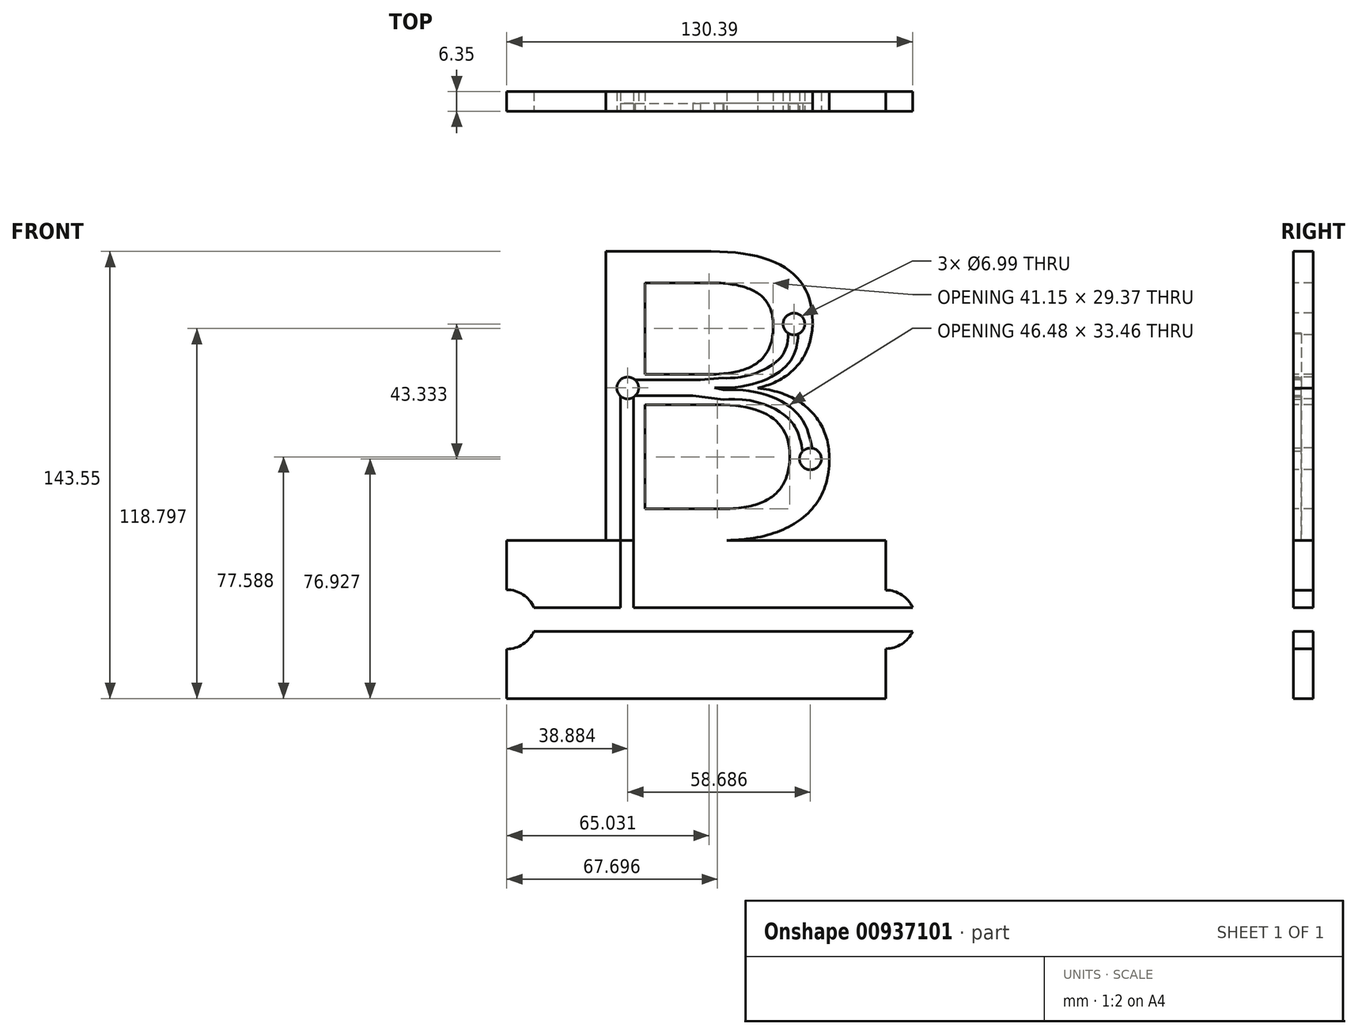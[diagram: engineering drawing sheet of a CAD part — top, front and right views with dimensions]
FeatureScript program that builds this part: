
annotation { "Feature Type Name" : "Feature", "Feature Type Description" : "" }
export const myFeature = defineFeature(function(context is Context, id is Id, definition is map)
    precondition{}
    {
        {
            var Q0;
            Q0=qCreatedBy(makeId("Front.planeOp"),FACE);
            var sketch = newSketch(context, id + "F0", { "sketchPlane" : qUnion([Q0])});
            skText(sketch, "E0", { "text": "B", "fontName": "Arimo-Regular.ttf"});
            skLineSegment(sketch, "E1", {"start": v(-24.82, -55) * mm, "end": v(-66.9, -55) * mm});
            skLineSegment(sketch, "E2", {"start": v(-66.9, -55) * mm, "end": v(-66.9, -70.87) * mm});
            skLineSegment(sketch, "E3", {"start": v(-66.9, -105.8) * mm, "end": v(54.89, -105.8) * mm});
            skLineSegment(sketch, "E4", {"start": v(54.89, -105.8) * mm, "end": v(54.89, -89.79) * mm});
            skLineSegment(sketch, "E5", {"start": v(54.89, -55) * mm, "end": v(0, -55) * mm});
            skArc(sketch, "E6", {"start": v(-66.9, -89.92) * mm, "mid": v(-57.38, -80.4) * mm, "end": v(-66.9, -70.87) * mm});
            skLineSegment(sketch, "E7.trimOffspring", {"start": v(-66.9, -89.92) * mm, "end": v(-66.9, -105.8) * mm});
            skArc(sketch, "E8", {"start": v(54.89, -89.79) * mm, "mid": v(64.29, -80.4) * mm, "end": v(54.89, -71) * mm});
            skLineSegment(sketch, "E9.trimOffspring", {"start": v(54.89, -71) * mm, "end": v(54.89, -55) * mm});
            skCircle(sketch, "E10", {"center": v(-28.03, -6.07) * mm, "radius": 3.5 * mm});
            skCircle(sketch, "E11", {"center": v(30.66, -28.86) * mm, "radius": 3.5 * mm});
            skCircle(sketch, "E12", {"center": v(25.36, 14.47) * mm, "radius": 3.5 * mm});
            skLineSegment(sketch, "E13", {"start": v(54.89, -80.4) * mm, "end": v(-66.9, -80.4) * mm, "construction": true});
            skLineSegment(sketch, "E14.0", {"start": v(64.2, -76.58) * mm, "end": v(-26.2, -76.58) * mm});
            skLineSegment(sketch, "E15.0", {"start": v(64.79, -84.2) * mm, "end": v(-69.35, -84.2) * mm});
            skLineSegment(sketch, "E16", {"start": v(-30.3, -3.53) * mm, "end": v(-30.3, -76.58) * mm});
            skLineSegment(sketch, "E17", {"start": v(-26.2, -76.58) * mm, "end": v(-26.2, -8.6) * mm});
            skLineSegment(sketch, "E18", {"start": v(-28.03, -6.07) * mm, "end": v(47.07, -6.07) * mm, "construction": true});
            skCircle(sketch, "E19", {"center": v(30.66, -28.86) * mm, "radius": 1.59 * mm, "construction": true});
            skFitSpline(sketch, "E20", {"points": [v(32.13, -28.02) * mm, v(31.78, -27.74) * mm, v(28.17, -16.54) * mm, v(2.65, -6.65) * mm], "startDerivative": vector(-5.04, 1.32) * mm, "endDerivative": vector(-61.91, -2.4) * mm});
            skCircle(sketch, "E21", {"center": v(25.36, 14.47) * mm, "radius": 1.59 * mm, "construction": true});
            skFitSpline(sketch, "E22", {"points": [v(26.72, 13.66) * mm, v(24.25, 2.64) * mm, v(2.53, -6.07) * mm], "startDerivative": vector(-0.47, -27.9) * mm, "endDerivative": vector(-51.33, 0) * mm});
            skLineSegment(sketch, "E23.0", {"start": v(-26.2, -8.6) * mm, "end": v(-7.1, -8.6) * mm});
            skLineSegment(sketch, "E24.0", {"start": v(-30.3, -3.53) * mm, "end": v(-4.72, -3.53) * mm});
            skFitSpline(sketch, "E25.0", {"points": [v(31.32, -31.09) * mm, v(31.28, -31.08) * mm, v(31.1, -31.03) * mm, v(30.71, -30.88) * mm, v(30.37, -30.7) * mm, v(30, -30.47) * mm, v(29.67, -30.18) * mm, v(29.38, -29.86) * mm, v(29.15, -29.54) * mm, v(29, -29.28) * mm, v(28.9, -29.08) * mm, v(28.82, -28.9) * mm, v(28.74, -28.7) * mm, v(28.64, -28.41) * mm, v(28.54, -28.09) * mm, v(28.45, -27.72) * mm, v(28.37, -27.34) * mm, v(28.26, -26.83) * mm, v(28.13, -26.14) * mm, v(27.95, -25.24) * mm, v(27.74, -24.28) * mm, v(27.5, -23.27) * mm, v(27.21, -22.23) * mm, v(26.87, -21.18) * mm, v(26.48, -20.16) * mm, v(26.1, -19.34) * mm, v(25.77, -18.71) * mm, v(25.5, -18.26) * mm, v(25.22, -17.83) * mm, v(24.82, -17.26) * mm, v(24.26, -16.57) * mm, v(23.5, -15.78) * mm, v(22.36, -14.77) * mm, v(20.72, -13.6) * mm, v(18.4, -12.39) * mm, v(14.9, -11.04) * mm, v(9.83, -9.92) * mm, v(5.19, -9.73) * mm, v(2.77, -9.82) * mm]});
            skFitSpline(sketch, "E26.0", {"points": [v(23.55, 13.71) * mm, v(23.53, 12.55) * mm, v(23.5, 10.88) * mm, v(23.3, 8.89) * mm, v(23.04, 7.51) * mm, v(22.64, 6.26) * mm, v(22.09, 5.09) * mm, v(21.33, 3.97) * mm, v(20.25, 2.82) * mm, v(18.87, 1.69) * mm, v(17.21, 0.61) * mm, v(15.29, -0.37) * mm, v(12.4, -1.52) * mm, v(8.26, -2.57) * mm, v(4.5, -2.9) * mm, v(2.53, -2.9) * mm]});
            skLineSegment(sketch, "E27", {"start": v(2.53, -2.9) * mm, "end": v(-4.72, -3.53) * mm});
            skLineSegment(sketch, "E28", {"start": v(2.83, -9.82) * mm, "end": v(-7.1, -8.6) * mm});
            skLineSegment(sketch, "E29", {"start": v(2.65, -6.65) * mm, "end": v(-0.2, -6.07) * mm});
            skLineSegment(sketch, "E30", {"start": v(-0.2, -6.07) * mm, "end": v(2.53, -6.07) * mm});
            skLineSegment(sketch, "E31", {"start": v(32, -27.99) * mm, "end": v(29.23, -29.65) * mm});
            skLineSegment(sketch, "E32", {"start": v(23.55, 13.64) * mm, "end": v(26.72, 13.66) * mm});
            skLineSegment(sketch, "E33.trimOffspring", {"start": v(-30.3, -76.58) * mm, "end": v(-69.35, -76.58) * mm});
            skLineSegment(sketch, "E34", {"start": v(-69.35, -84.2) * mm, "end": v(-69.35, -76.58) * mm});
            skLineSegment(sketch, "E35", {"start": v(64.79, -84.2) * mm, "end": v(64.79, -75.52) * mm});
            const initialGuessF0  = {"E0": [-0.04609, -0.055, 1, 0, 0.09708]};
            skSetInitialGuess(sketch, initialGuessF0);
            skSolve(sketch);
        }
        {
            var Q0;
            Q0=makeQuery(id+"F0.imprint","IMPRINT",FACE,{"disambiguationData":[TD([[makeQuery(id+"F0.imprint","IMPRINT",EDGE,{"derivedFrom":sQuery(id+"F0.wireOp",EDGE,"E0.sketch_text.stroke-0")}),-1.0]])]});
            var Q1;
            {var subQ2=sQuery(id+"F0.wireOp",EDGE,"E0.sketch_text.stroke-2");Q1=makeQuery(id+"F0.imprint","IMPRINT",FACE,{"disambiguationData":[TD([[makeQuery(id+"F0.imprint","IMPRINT",EDGE,{"derivedFrom":subQ2}),1.0]])]});}
            var Q2;
            {var subQ1=sQuery(id+"F0.wireOp",EDGE,"E2");Q2=makeQuery(id+"F0.imprint","IMPRINT",FACE,{"disambiguationData":[TD([[makeQuery(id+"F0.imprint","IMPRINT",EDGE,{"derivedFrom":subQ1}),1.0]])]});}
            var Q3;
            Q3=makeQuery(id+"F0.imprint","IMPRINT",FACE,{"disambiguationData":[TD([[makeQuery(id+"F0.imprint","IMPRINT",EDGE,{"derivedFrom":sQuery(id+"F0.wireOp",EDGE,"E3")}),1.0]])]});
            var Q4;
            {var subQ5=sQuery(id+"F0.wireOp",EDGE,"E17");var subQ11=sQuery(id+"F0.wireOp",EDGE,"E1");var subQ12=makeQuery(id+"F0.imprint","INTERSECT",VERTEX,{"derivedFrom":[subQ11,subQ5]});Q4=makeQuery(id+"F0.imprint","IMPRINT",FACE,{"disambiguationData":[TD([[makeQuery(id+"F0.imprint","IMPRINT",EDGE,{"disambiguationData":[TD([[subQ12,-1.0]])],"derivedFrom":subQ11}),1.0]])]});}
            var Q5;
            {var subQ0=sQuery(id+"F0.wireOp",EDGE,"E17");var subQ1=sQuery(id+"F0.wireOp",EDGE,"E1");var subQ2=makeQuery(id+"F0.imprint","INTERSECT",VERTEX,{"derivedFrom":[subQ1,subQ0]});Q5=makeQuery(id+"F0.imprint","IMPRINT",FACE,{"disambiguationData":[TD([[makeQuery(id+"F0.imprint","IMPRINT",EDGE,{"disambiguationData":[TD([[subQ2,-1.0]])],"derivedFrom":subQ1}),-1.0]])]});}
            var Q6;
            {var subQ0=sQuery(id+"F0.wireOp",EDGE,"E27");Q6=makeQuery(id+"F0.imprint","IMPRINT",FACE,{"disambiguationData":[TD([[makeQuery(id+"F0.imprint","IMPRINT",EDGE,{"derivedFrom":subQ0}),1.0]])]});}
            extrude(context, id + "F1", {"entities" : qUnion([Q0, Q1, Q2, Q3, Q4, Q5, Q6]), "oppositeDirection" : true, "depth" : 6.35 * mm, "offsetDistance" : 25.4 * mm});
        }
        {
            var Q0;
            {var subQ5=sQuery(id+"F0.wireOp",EDGE,"E17");var subQ11=sQuery(id+"F0.wireOp",EDGE,"E1");var subQ12=makeQuery(id+"F0.imprint","INTERSECT",VERTEX,{"derivedFrom":[subQ11,subQ5]});Q0=makeQuery(id+"F0.imprint","IMPRINT",FACE,{"disambiguationData":[TD([[makeQuery(id+"F0.imprint","IMPRINT",EDGE,{"disambiguationData":[TD([[subQ12,-1.0]])],"derivedFrom":subQ11}),1.0]])]});}
            var Q1;
            {var subQ0=sQuery(id+"F0.wireOp",EDGE,"E17");var subQ1=sQuery(id+"F0.wireOp",EDGE,"E1");var subQ2=makeQuery(id+"F0.imprint","INTERSECT",VERTEX,{"derivedFrom":[subQ1,subQ0]});Q1=makeQuery(id+"F0.imprint","IMPRINT",FACE,{"disambiguationData":[TD([[makeQuery(id+"F0.imprint","IMPRINT",EDGE,{"disambiguationData":[TD([[subQ2,-1.0]])],"derivedFrom":subQ1}),-1.0]])]});}
            var Q2;
            {var subQ0=sQuery(id+"F0.wireOp",EDGE,"E27");Q2=makeQuery(id+"F0.imprint","IMPRINT",FACE,{"disambiguationData":[TD([[makeQuery(id+"F0.imprint","IMPRINT",EDGE,{"derivedFrom":subQ0}),1.0]])]});}
            extrude(context, id + "F2", {"entities" : qUnion([Q0, Q1, Q2]), "operationType" : NewBodyOperationType.REMOVE, "oppositeDirection" : true, "depth" : 2.54 * mm, "offsetDistance" : 25.4 * mm});
        }
    });
